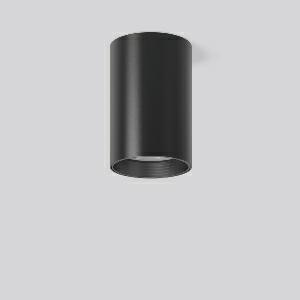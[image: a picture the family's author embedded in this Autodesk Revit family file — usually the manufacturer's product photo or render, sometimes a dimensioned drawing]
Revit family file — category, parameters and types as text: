
# Revit family: heledon_maxi_a_931221_003_3_a274
name_source: partatom
category: Lighting Fixtures
units: mm (PartAtom-declared; Revit-internal decimal feet)

## family parameters
Cut with Voids When Loaded = No
Host = Face
Light Source = No
Part Type = Normal
Room Calculation Point = No
Round Connector Dimension = Use Diameter
Shared = No

## types (1)
- HELEDON maxi A (1 x LED Modul 935, 2800 lm, 3500)
    Apparent Load = 25 VA
    Approval mark = CE
    CIE Flux Codes = 96 100 100 100 100
    Color Rendering = 92
    Color Temperature = 3500
    Default Elevation = 1800 mm
    Description = Series: HELEDON maxi
Cylindrical surface-mounted downlight. Housing: die-cast aluminium, powder-coated. Internal ceiling frame polycarbonate with bayonet mounting. Black plastic ring and recessed LED to prevent glare from the side. Optical assembly with lens made of plastic (polycarbonate) for the best homogeneous light distribution - can be changed without tools. Best colour rendering index Ra>90. Suitable for Ceiling mounting. Easy installation with a separate ceiling frame with bayonet mounting and plug connection. Driver integrated. Connected via plug-in connector. High quality converter without flickering and stroboscopic effect. The following accessories can be mounted without use of tools: interchangeable lenses, decorative glasses, honeycomb louvre, clear and frosted diffusers, white interchangeable plastic ring. 
Colour: deep black, matt (RAL 9005)
Diameter: 123 mm
Height: 183 mm
Lamp: LED
Socket: without socket
Colour temperature: 3500K
Colour rendering index (CRI): 92
System power: 25 W
Rated luminous flux: 2800 lm
Luminous efficiency: 112 lm/W
Control gear: Regulated power supply
Protection class: I
Type of protection: IP 20
    Height = 183 mm
    Lamp = 1 x LED Modul 935
    Lamp Light Flux = 2800 lm
    Lamp count = 1
    Length = 123 mm
    Lifetime = 50000 h
    Luminous efficacy = 112 lm/W
    Manufacturer = RZB
    ModVariant = No
    Model = 931221.003.3
    Mounting Place = Ceiling
    Mounting Type = Surface mounted
    Number of Poles = 1
    OnlyDefault = Yes
    Power Factor = 1
    Product Name = HELEDON maxi A
    Product group = Surface mounted downlights
    ProductGroupID = 302
    Protection Class = Protection class I
    Protection Degree = IP 20
    RLX_Detail_Level = 1
    RLX_Emergency_Light_Flux = 0 lm
    RLX_Emergency_Type = 0
    RLX_Emergency_Type_DB = No
    RlxData = <blob elided: 99177 chars, md5=e2f27396>
    Socket = socket
    Standby Power = 0 W
    System Light Flux = 2800 lm
    System Power = 25 W
    Type Comments = Product without accessories
    Type Image = 931193.003.jpg
    URL = http://relux.com
    VarID = ---
    Voltage = 230 V
    Voltage Range = 220-240 V
    Weight = 0.00 kg
    Width = 0 mm  [stored 0 ft]

note: [stored X ft] marks values corroborated as IEEE doubles in the binary element streams (Revit-internal decimal feet)

## geometry (parser evidence)
native form markers: Blend x4, Sweep x11
no freeform markers — native parametric forms only
